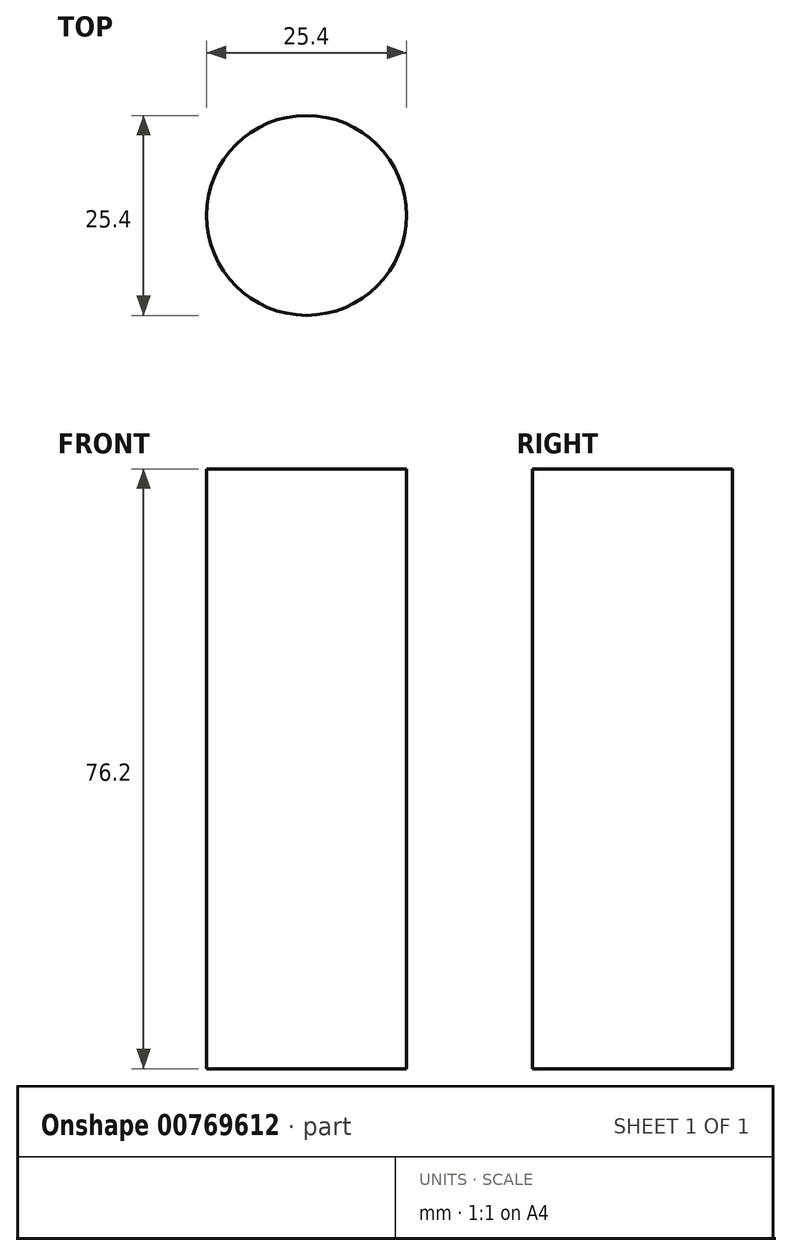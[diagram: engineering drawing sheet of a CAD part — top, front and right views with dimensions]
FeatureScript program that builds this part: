
annotation { "Feature Type Name" : "Feature", "Feature Type Description" : "" }
export const myFeature = defineFeature(function(context is Context, id is Id, definition is map)
    precondition{}
    {
        {
            var Q0;
            Q0=qCreatedBy(makeId("Top.planeOp"),FACE);
            var sketch = newSketch(context, id + "F0", { "sketchPlane" : qUnion([Q0])});
            skCircle(sketch, "E0", {"center": v(0, 0) * mm, "radius": 12.7 * mm});
            skSolve(sketch);
        }
        {
            var Q0;
            Q0 = qSketchRegion(id + "F0", true);
            extrude(context, id + "F1", {"entities" : qUnion([Q0]), "depth" : 76.2 * mm, "offsetDistance" : 25 * mm});
        }
    });
